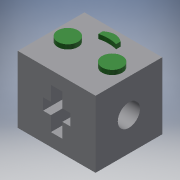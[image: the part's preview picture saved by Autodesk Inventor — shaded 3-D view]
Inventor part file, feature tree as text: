
AUTODESK INVENTOR PART (.ipt)
format: ipt  version: 2019 (Build 230136000, 136)  size: 168,960 bytes
history: native  units: mm
features: other x4, extrude x4, sketch x4, projected_geometry x2, reference x1
ambient origin geometry x8: Origin, YZ Plane, XZ Plane, XY Plane, X Axis, Y Axis, Z Axis, Center Point
bodies: Body1 (feature_tree)
feature tree (15):
  other  "ソリッド1"
  extrude  "押し出し1"  Depth=35.0mm
  extrude  "押し出し2"  Depth=30.0mm
  extrude  "押し出し3"  Depth=30.0mm TaperAngle=0.0deg
  extrude  "顔"  Depth=10.0mm
  sketch  "スケッチ1"
  sketch  "スケッチ4"
  projected_geometry  "投影ループ2"
  sketch  "スケッチ5"
  reference  "参照1"
  sketch  "スケッチ6"
  projected_geometry  "投影ループ3"
  other  "<userpath>\OneDrive\デスクトップ\mini_robot\mini_robot.iam"
  other  "mini_robot.iam"
  other  "body:1"
